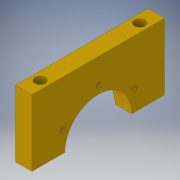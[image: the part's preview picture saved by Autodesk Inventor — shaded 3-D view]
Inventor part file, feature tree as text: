
AUTODESK INVENTOR PART (.ipt)
format: ipt  version: 2019.3 (Build 233278000, 278)  size: 137,728 bytes
history: native  units: in
note: dims shown in document units (in); Inventor stores cm internally (conversion verified against a paired STEP export)
features: sketch x4, extrude x2, hole x2
ambient origin geometry x8: Origin, YZ Plane, XZ Plane, XY Plane, X Axis, Y Axis, Z Axis, Center Point
bodies: Solid1 (feature_tree)
feature tree (8):
  extrude  "Extrusion1"  Depth=2.0in
  hole  "Hole2"  [1 undecoded]
  hole  "Hole3"  [1 undecoded]
  extrude  "Extrusion2"  Depth=0.5in
  sketch  "Sketch1"  dims[d0=4.0in d1=2.0in]
  sketch  "Sketch3"  dims[d2=2.02in d3=0.5in d4=0.0in]
  sketch  "Sketch4"  dims[d6=2.0in d7=2.0in]
  sketch  "Sketch5"  dims[d15=2.3622in d17=360.0deg d19=0.15in d20=0.75in d21=0.279in d22=0.25in d23=0.5635in d24=1.0in d25=0.8108in d26=0.5in d27=0.5in d28=0.266in d29=0.75in d30=0.507in d31=0.25in d32=0.5635in d33=1.0in d34=0.8108in d35=0.316in d36=0.5in d37=0.0in]
note: 2 required parameter values undecoded (feature->parameter linkage not recoverable at this tier; creation-order binding heuristic only, values carry confidence <= 0.55)
